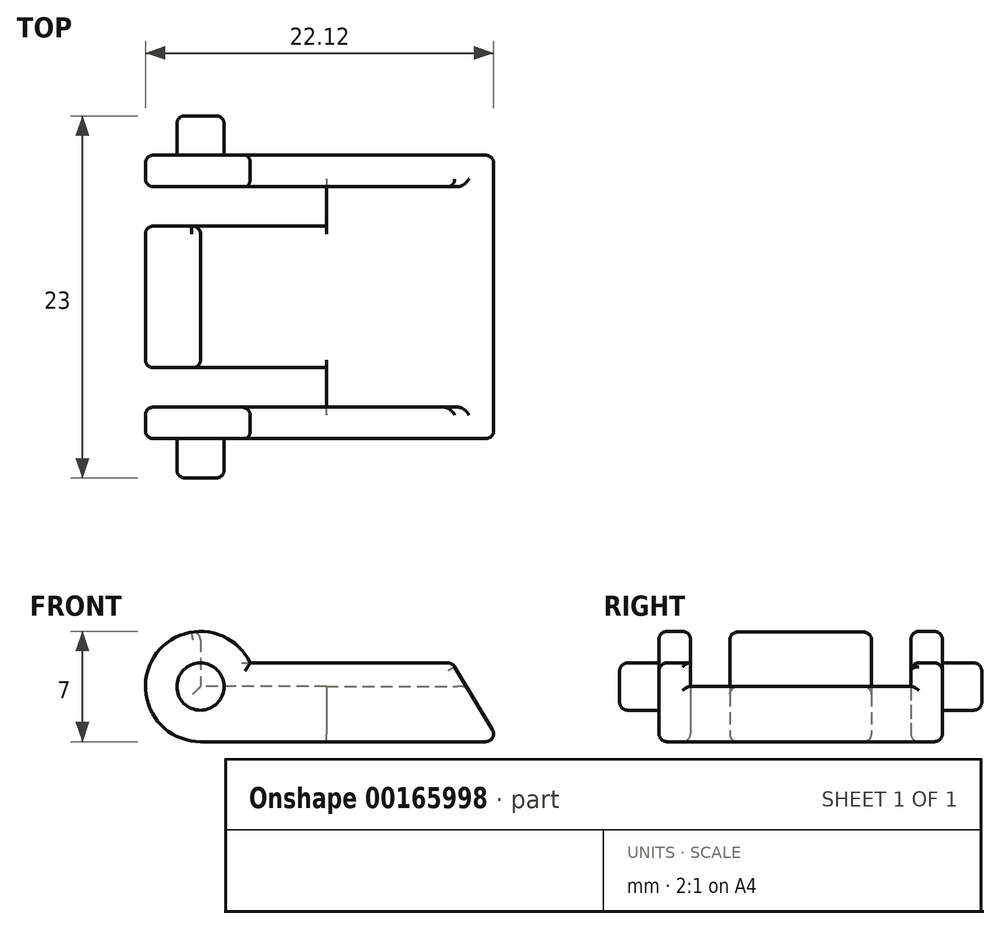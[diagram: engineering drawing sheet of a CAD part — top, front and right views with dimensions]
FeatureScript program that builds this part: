
annotation { "Feature Type Name" : "Feature", "Feature Type Description" : "" }
export const myFeature = defineFeature(function(context is Context, id is Id, definition is map)
    precondition{}
    {
        {
            var Q0;
            Q0=qCreatedBy(makeId("Front.planeOp"),FACE);
            var sketch = newSketch(context, id + "F0", { "sketchPlane" : qUnion([Q0])});
            skLineSegment(sketch, "E0.bottom", {"start": v(0, 0) * mm, "end": v(19, 0) * mm});
            skLineSegment(sketch, "E0.left", {"start": v(0, 0) * mm, "end": v(0, 5) * mm});
            skLineSegment(sketch, "E1", {"start": v(0, 5) * mm, "end": v(16, 5) * mm});
            skLineSegment(sketch, "E2", {"start": v(16, 5) * mm, "end": v(19, 0) * mm});
            skLineSegment(sketch, "E3", {"start": v(0, 0) * mm, "end": v(0, 3.5) * mm});
            skCircle(sketch, "E4", {"center": v(0, 3.5) * mm, "radius": 3.5 * mm});
            skSolve(sketch);
        }
        {
            var Q0;
            {var subQ0=sQuery(id+"F0.wireOp",EDGE,"E0.left");Q0=makeQuery(id+"F0.imprint","IMPRINT",FACE,{"disambiguationData":[TD([[makeQuery(id+"F0.imprint","IMPRINT",EDGE,{"derivedFrom":subQ0}),1.0]])]});}
            var Q1;
            {var subQ0=sQuery(id+"F0.wireOp",EDGE,"E0.left");Q1=makeQuery(id+"F0.imprint","IMPRINT",FACE,{"disambiguationData":[TD([[makeQuery(id+"F0.imprint","IMPRINT",EDGE,{"derivedFrom":subQ0}),-1.0]])]});}
            var Q2;
            {var subQ0=sQuery(id+"F0.wireOp",EDGE,"E0.bottom");Q2=makeQuery(id+"F0.imprint","IMPRINT",FACE,{"disambiguationData":[TD([[makeQuery(id+"F0.imprint","IMPRINT",EDGE,{"derivedFrom":subQ0}),1.0]])]});}
            extrude(context, id + "F1", {"entities" : qUnion([Q0, Q1, Q2]), "depth" : 18 * mm});
        }
        {
            var Q0;
            Q0=makeQuery(id+"F1.opExtrude","CAP_FACE",FACE,{"disambiguationData":[OSD([sQuery(id+"F0.wireOp",EDGE,"E0.bottom"),sQuery(id+"F0.wireOp",EDGE,"E1"),sQuery(id+"F0.wireOp",EDGE,"E2"),sQuery(id+"F0.wireOp",EDGE,"E4")])],"isStart":false});
            var sketch = newSketch(context, id + "F2", { "sketchPlane" : qUnion([Q0])});
            skCircle(sketch, "E5", {"center": v(0, 3.5) * mm, "radius": 1.5 * mm});
            skSolve(sketch);
        }
        {
            var Q0;
            Q0=makeQuery(id+"F2.imprint","IMPRINT",FACE,{"disambiguationData":[TD([[makeQuery(id+"F2.imprint","IMPRINT",EDGE,{"derivedFrom":sQuery(id+"F2.wireOp",EDGE,"E5")}),1.0]])]});
            extrude(context, id + "F3", {"entities" : qUnion([Q0]), "operationType" : NewBodyOperationType.ADD, "depth" : 2.5 * mm});
        }
        {
            var Q0;
            Q0=makeQuery(id+"F1.opExtrude","CAP_FACE",FACE,{"disambiguationData":[OSD([sQuery(id+"F0.wireOp",EDGE,"E0.bottom"),sQuery(id+"F0.wireOp",EDGE,"E1"),sQuery(id+"F0.wireOp",EDGE,"E2"),sQuery(id+"F0.wireOp",EDGE,"E4")])],"isStart":true});
            var sketch = newSketch(context, id + "F4", { "sketchPlane" : qUnion([Q0])});
            skCircle(sketch, "E6", {"center": v(0, 3.5) * mm, "radius": 1.5 * mm});
            skSolve(sketch);
        }
        {
            var Q0;
            Q0=makeQuery(id+"F4.imprint","IMPRINT",FACE,{"disambiguationData":[TD([[makeQuery(id+"F4.imprint","IMPRINT",EDGE,{"derivedFrom":sQuery(id+"F4.wireOp",EDGE,"E6")}),1.0]])]});
            extrude(context, id + "F5", {"entities" : qUnion([Q0]), "operationType" : NewBodyOperationType.ADD, "depth" : 2.5 * mm});
        }
        {
            var Q0;
            Q0=makeQuery(id+"F1.opExtrude","SWEPT_FACE",FACE,{"disambiguationData":[OSD([sQuery(id+"F0.wireOp",EDGE,"E0.bottom")])]});
            var sketch = newSketch(context, id + "F6", { "sketchPlane" : qUnion([Q0])});
            skLineSegment(sketch, "E7.bottom", {"start": v(8, 13.5) * mm, "end": v(-8, 13.5) * mm});
            skLineSegment(sketch, "E7.top", {"start": v(8, 16) * mm, "end": v(-8, 16) * mm});
            skLineSegment(sketch, "E7.left", {"start": v(8, 13.5) * mm, "end": v(8, 16) * mm});
            skLineSegment(sketch, "E7.right", {"start": v(-8, 13.5) * mm, "end": v(-8, 16) * mm});
            skPoint(sketch, "E7.middle", {"position": v(0, 14.75) * mm});
            skLineSegment(sketch, "E8.bottom", {"start": v(8, 4.5) * mm, "end": v(-8, 4.5) * mm});
            skLineSegment(sketch, "E8.top", {"start": v(8, 2) * mm, "end": v(-8, 2) * mm});
            skLineSegment(sketch, "E8.left", {"start": v(8, 4.5) * mm, "end": v(8, 2) * mm});
            skLineSegment(sketch, "E8.right", {"start": v(-8, 4.5) * mm, "end": v(-8, 2) * mm});
            skPoint(sketch, "E8.middle", {"position": v(0, 3.3) * mm});
            skSolve(sketch);
        }
        {
            var Q0;
            Q0 = qSketchRegion(id + "F6", true);
            extrude(context, id + "F7", {"entities" : qUnion([Q0]), "operationType" : NewBodyOperationType.REMOVE, "endBound" : BoundingType.THROUGH_ALL, "oppositeDirection" : true, "depth" : 25 * mm});
        }
        {
            var Q0;
            Q0=makeQuery(id+"F1.opExtrude","SWEPT_FACE",FACE,{"disambiguationData":[OSD([sQuery(id+"F0.wireOp",EDGE,"E1")])]});
            var sketch = newSketch(context, id + "F8", { "sketchPlane" : qUnion([Q0])});
            skLineSegment(sketch, "E9.bottom", {"start": v(0, -2) * mm, "end": v(18.99, -2) * mm});
            skLineSegment(sketch, "E9.top", {"start": v(0, -16) * mm, "end": v(18.99, -16) * mm});
            skLineSegment(sketch, "E9.left", {"start": v(0, -2) * mm, "end": v(0, -16) * mm});
            skLineSegment(sketch, "E9.right", {"start": v(18.99, -2) * mm, "end": v(18.99, -16) * mm});
            skSolve(sketch);
        }
        {
            var Q0;
            Q0 = qSketchRegion(id + "F8", true);
            extrude(context, id + "F9", {"entities" : qUnion([Q0]), "operationType" : NewBodyOperationType.REMOVE, "oppositeDirection" : true, "depth" : 1.5 * mm});
        }
        {
            var Q0;
            Q0=makeQuery(id+"F9.boolean.opBoolean","COPY",FACE,{"derivedFrom":makeQuery(id+"F9.opExtrude","CAP_FACE",FACE,{"disambiguationData":[OSD([sQuery(id+"F8.wireOp",EDGE,"E9.bottom"),sQuery(id+"F8.wireOp",EDGE,"E9.top"),sQuery(id+"F8.wireOp",EDGE,"E9.left"),sQuery(id+"F8.wireOp",EDGE,"E9.right")])],"isStart":false})});
            var sketch = newSketch(context, id + "F10", { "sketchPlane" : qUnion([Q0])});
            skLineSegment(sketch, "E10.bottom", {"start": v(0, -4.5) * mm, "end": v(4.86, -4.5) * mm});
            skLineSegment(sketch, "E10.top", {"start": v(0, -13.5) * mm, "end": v(4.86, -13.5) * mm});
            skLineSegment(sketch, "E10.left", {"start": v(0, -4.5) * mm, "end": v(0, -13.5) * mm});
            skLineSegment(sketch, "E10.right", {"start": v(4.86, -4.5) * mm, "end": v(4.86, -13.5) * mm});
            skSolve(sketch);
        }
        {
            var Q0;
            Q0 = qSketchRegion(id + "F10", true);
            extrude(context, id + "F11", {"entities" : qUnion([Q0]), "operationType" : NewBodyOperationType.REMOVE, "depth" : 6.3 * mm});
        }
        {
            var Q0;
            Q0=makeQuery(id+"F1.opExtrude","CAP_EDGE",EDGE,{"disambiguationData":[OSD([sQuery(id+"F0.wireOp",EDGE,"E1")])],"isStart":false});
            var Q1;
            Q1=makeQuery(id+"F1.opExtrude","CAP_EDGE",EDGE,{"disambiguationData":[OSD([sQuery(id+"F0.wireOp",EDGE,"E2")])],"isStart":false});
            var Q2;
            Q2=makeQuery(id+"F1.opExtrude","CAP_EDGE",EDGE,{"disambiguationData":[OSD([sQuery(id+"F0.wireOp",EDGE,"E0.bottom")])],"isStart":false});
            var Q3;
            Q3=makeQuery(id+"F9.boolean.opBoolean","INTERSECT",EDGE,{"derivedFrom":[makeQuery(id+"F1.opExtrude","SWEPT_FACE",FACE,{"disambiguationData":[OSD([sQuery(id+"F0.wireOp",EDGE,"E2")])]}),makeQuery(id+"F9.opExtrude","SWEPT_FACE",FACE,{"disambiguationData":[OSD([sQuery(id+"F8.wireOp",EDGE,"E9.top")])]})]});
            var Q4;
            Q4=makeQuery(id+"F9.boolean.opBoolean","INTERSECT",EDGE,{"derivedFrom":[makeQuery(id+"F1.opExtrude","SWEPT_FACE",FACE,{"disambiguationData":[OSD([sQuery(id+"F0.wireOp",EDGE,"E2")])]}),makeQuery(id+"F9.opExtrude","CAP_FACE",FACE,{"disambiguationData":[OSD([sQuery(id+"F8.wireOp",EDGE,"E9.bottom"),sQuery(id+"F8.wireOp",EDGE,"E9.top"),sQuery(id+"F8.wireOp",EDGE,"E9.left"),sQuery(id+"F8.wireOp",EDGE,"E9.right")])],"isStart":false})]});
            var Q5;
            {var subQ0=sQuery(id+"F0.wireOp",EDGE,"E2");var subQ1=sQuery(id+"F0.wireOp",EDGE,"E1");Q5=makeQuery(id+"F9.boolean.opBoolean","SPLIT",EDGE,{"disambiguationData":[TD([makeQuery(id+"F9.opExtrude","SWEPT_FACE",FACE,{"disambiguationData":[OSD([sQuery(id+"F8.wireOp",EDGE,"E9.top")])]})])],"derivedFrom":makeQuery(id+"F1.opExtrude","SWEPT_EDGE",EDGE,{"disambiguationData":[OSD([subQ1,subQ0])]})});}
            var Q6;
            Q6=makeQuery(id+"F9.boolean.opBoolean","INTERSECT",EDGE,{"derivedFrom":[makeQuery(id+"F7.boolean.opBoolean","COPY",FACE,{"derivedFrom":makeQuery(id+"F7.opExtrude","SWEPT_FACE",FACE,{"disambiguationData":[OSD([sQuery(id+"F6.wireOp",EDGE,"E7.bottom")])]})}),makeQuery(id+"F9.opExtrude","CAP_FACE",FACE,{"disambiguationData":[OSD([sQuery(id+"F8.wireOp",EDGE,"E9.bottom"),sQuery(id+"F8.wireOp",EDGE,"E9.top"),sQuery(id+"F8.wireOp",EDGE,"E9.left"),sQuery(id+"F8.wireOp",EDGE,"E9.right")])],"isStart":false})]});
            var Q7;
            Q7=makeQuery(id+"F11.boolean.opBoolean","MERGE",EDGE,{"derivedFrom":[makeQuery(id+"F9.boolean.opBoolean","INTERSECT",EDGE,{"derivedFrom":[makeQuery(id+"F7.boolean.opBoolean","COPY",FACE,{"derivedFrom":makeQuery(id+"F7.opExtrude","SWEPT_FACE",FACE,{"disambiguationData":[OSD([sQuery(id+"F6.wireOp",EDGE,"E7.bottom")])]})}),makeQuery(id+"F9.opExtrude","SWEPT_FACE",FACE,{"disambiguationData":[OSD([sQuery(id+"F8.wireOp",EDGE,"E9.left")])]})]}),makeQuery(id+"F11.opExtrude","SWEPT_EDGE",EDGE,{"disambiguationData":[OSD([sQuery(id+"F10.wireOp",EDGE,"E10.top"),sQuery(id+"F10.wireOp",EDGE,"E10.left")])]})]});
            var Q8;
            Q8=makeQuery(id+"F11.boolean.opBoolean","MERGE",EDGE,{"derivedFrom":[makeQuery(id+"F9.boolean.opBoolean","INTERSECT",EDGE,{"derivedFrom":[makeQuery(id+"F7.boolean.opBoolean","COPY",FACE,{"derivedFrom":makeQuery(id+"F7.opExtrude","SWEPT_FACE",FACE,{"disambiguationData":[OSD([sQuery(id+"F6.wireOp",EDGE,"E8.bottom")])]})}),makeQuery(id+"F9.opExtrude","SWEPT_FACE",FACE,{"disambiguationData":[OSD([sQuery(id+"F8.wireOp",EDGE,"E9.left")])]})]}),makeQuery(id+"F11.opExtrude","SWEPT_EDGE",EDGE,{"disambiguationData":[OSD([sQuery(id+"F10.wireOp",EDGE,"E10.bottom"),sQuery(id+"F10.wireOp",EDGE,"E10.left")])]})]});
            var Q9;
            Q9=makeQuery(id+"F9.boolean.opBoolean","INTERSECT",EDGE,{"derivedFrom":[makeQuery(id+"F7.boolean.opBoolean","COPY",FACE,{"derivedFrom":makeQuery(id+"F7.opExtrude","SWEPT_FACE",FACE,{"disambiguationData":[OSD([sQuery(id+"F6.wireOp",EDGE,"E8.bottom")])]})}),makeQuery(id+"F9.opExtrude","CAP_FACE",FACE,{"disambiguationData":[OSD([sQuery(id+"F8.wireOp",EDGE,"E9.bottom"),sQuery(id+"F8.wireOp",EDGE,"E9.top"),sQuery(id+"F8.wireOp",EDGE,"E9.left"),sQuery(id+"F8.wireOp",EDGE,"E9.right")])],"isStart":false})]});
            var Q10;
            {var subQ0=sQuery(id+"F0.wireOp",EDGE,"E2");var subQ1=sQuery(id+"F0.wireOp",EDGE,"E1");Q10=makeQuery(id+"F9.boolean.opBoolean","SPLIT",EDGE,{"disambiguationData":[TD([makeQuery(id+"F9.opExtrude","SWEPT_FACE",FACE,{"disambiguationData":[OSD([sQuery(id+"F8.wireOp",EDGE,"E9.bottom")])]})])],"derivedFrom":makeQuery(id+"F1.opExtrude","SWEPT_EDGE",EDGE,{"disambiguationData":[OSD([subQ1,subQ0])]})});}
            var Q11;
            Q11=makeQuery(id+"F1.opExtrude","CAP_EDGE",EDGE,{"disambiguationData":[OSD([sQuery(id+"F0.wireOp",EDGE,"E2")])],"isStart":true});
            var Q12;
            Q12=makeQuery(id+"F1.opExtrude","SWEPT_EDGE",EDGE,{"disambiguationData":[OSD([sQuery(id+"F0.wireOp",EDGE,"E0.bottom"),sQuery(id+"F0.wireOp",EDGE,"E2")])]});
            var Q13;
            Q13=makeQuery(id+"F9.boolean.opBoolean","INTERSECT",EDGE,{"derivedFrom":[makeQuery(id+"F1.opExtrude","SWEPT_FACE",FACE,{"disambiguationData":[OSD([sQuery(id+"F0.wireOp",EDGE,"E2")])]}),makeQuery(id+"F9.opExtrude","SWEPT_FACE",FACE,{"disambiguationData":[OSD([sQuery(id+"F8.wireOp",EDGE,"E9.bottom")])]})]});
            var Q14;
            Q14=makeQuery(id+"F1.opExtrude","CAP_EDGE",EDGE,{"disambiguationData":[OSD([sQuery(id+"F0.wireOp",EDGE,"E1")])],"isStart":true});
            var Q15;
            Q15=makeQuery(id+"F1.opExtrude","CAP_EDGE",EDGE,{"disambiguationData":[OSD([sQuery(id+"F0.wireOp",EDGE,"E4")])],"isStart":true});
            var Q16;
            Q16=makeQuery(id+"F7.boolean.opBoolean","INTERSECT",EDGE,{"derivedFrom":[makeQuery(id+"F1.opExtrude","SWEPT_FACE",FACE,{"disambiguationData":[OSD([sQuery(id+"F0.wireOp",EDGE,"E4")])]}),makeQuery(id+"F7.opExtrude","SWEPT_FACE",FACE,{"disambiguationData":[OSD([sQuery(id+"F6.wireOp",EDGE,"E7.top")])]})]});
            var Q17;
            Q17=makeQuery(id+"F7.boolean.opBoolean","INTERSECT",EDGE,{"derivedFrom":[makeQuery(id+"F1.opExtrude","SWEPT_FACE",FACE,{"disambiguationData":[OSD([sQuery(id+"F0.wireOp",EDGE,"E4")])]}),makeQuery(id+"F7.opExtrude","SWEPT_FACE",FACE,{"disambiguationData":[OSD([sQuery(id+"F6.wireOp",EDGE,"E8.top")])]})]});
            var Q18;
            Q18=makeQuery(id+"F3.opExtrude","CAP_EDGE",EDGE,{"disambiguationData":[OSD([sQuery(id+"F2.wireOp",EDGE,"E5")])],"isStart":false});
            var Q19;
            Q19=makeQuery(id+"F5.opExtrude","CAP_EDGE",EDGE,{"disambiguationData":[OSD([sQuery(id+"F4.wireOp",EDGE,"E6")])],"isStart":false});
            var Q20;
            Q20=makeQuery(id+"F7.boolean.opBoolean","INTERSECT",EDGE,{"derivedFrom":[makeQuery(id+"F1.opExtrude","SWEPT_FACE",FACE,{"disambiguationData":[OSD([sQuery(id+"F0.wireOp",EDGE,"E4")])]}),makeQuery(id+"F7.opExtrude","SWEPT_FACE",FACE,{"disambiguationData":[OSD([sQuery(id+"F6.wireOp",EDGE,"E8.bottom")])]})]});
            var Q21;
            Q21=makeQuery(id+"F7.boolean.opBoolean","INTERSECT",EDGE,{"derivedFrom":[makeQuery(id+"F1.opExtrude","SWEPT_FACE",FACE,{"disambiguationData":[OSD([sQuery(id+"F0.wireOp",EDGE,"E4")])]}),makeQuery(id+"F7.opExtrude","SWEPT_FACE",FACE,{"disambiguationData":[OSD([sQuery(id+"F6.wireOp",EDGE,"E7.bottom")])]})]});
            fillet(context, id + "F12", {"entities" : qUnion([Q0, Q1, Q2, Q3, Q4, Q5, Q6, Q7, Q8, Q9, Q10, Q11, Q12, Q13, Q14, Q15, Q16, Q17, Q18, Q19, Q20, Q21]), "radius" : .5 * mm, "tangentPropagation" : true, "allowEdgeOverflow" : false});
        }
        {
            var Q0;
            Q0=makeQuery(id+"F7.boolean.opBoolean","INTERSECT",EDGE,{"derivedFrom":[makeQuery(id+"F1.opExtrude","SWEPT_FACE",FACE,{"disambiguationData":[OSD([sQuery(id+"F0.wireOp",EDGE,"E1")])]}),makeQuery(id+"F7.opExtrude","SWEPT_FACE",FACE,{"disambiguationData":[OSD([sQuery(id+"F6.wireOp",EDGE,"E8.top")])]})]});
            var Q1;
            Q1=makeQuery(id+"F9.boolean.opBoolean","MERGE",EDGE,{"derivedFrom":[makeQuery(id+"F7.boolean.opBoolean","INTERSECT",EDGE,{"derivedFrom":[makeQuery(id+"F1.opExtrude","SWEPT_FACE",FACE,{"disambiguationData":[OSD([sQuery(id+"F0.wireOp",EDGE,"E1")])]}),makeQuery(id+"F7.opExtrude","SWEPT_FACE",FACE,{"disambiguationData":[OSD([sQuery(id+"F6.wireOp",EDGE,"E7.top")])]})]}),makeQuery(id+"F9.opExtrude","CAP_EDGE",EDGE,{"disambiguationData":[OSD([sQuery(id+"F8.wireOp",EDGE,"E9.top")])],"isStart":true})]});
            fillet(context, id + "F13", {"entities" : qUnion([Q0, Q1]), "radius" : .5 * mm, "tangentPropagation" : true, "allowEdgeOverflow" : false});
        }
        {
            var Q0;
            Q0=makeQuery(id+"F11.boolean.opBoolean","INTERSECT",EDGE,{"derivedFrom":[makeQuery(id+"F7.boolean.opBoolean","SPLIT",FACE,{"disambiguationData":[TD([makeQuery(id+"F7.opExtrude","SWEPT_FACE",FACE,{"disambiguationData":[OSD([sQuery(id+"F6.wireOp",EDGE,"E7.bottom")])]})])],"derivedFrom":makeQuery(id+"F1.opExtrude","SWEPT_FACE",FACE,{"disambiguationData":[OSD([sQuery(id+"F0.wireOp",EDGE,"E4")])]})}),makeQuery(id+"F11.opExtrude","SWEPT_FACE",FACE,{"disambiguationData":[OSD([sQuery(id+"F10.wireOp",EDGE,"E10.left")])]})]});
            fillet(context, id + "F14", {"entities" : qUnion([Q0]), "radius" : .5 * mm, "tangentPropagation" : true, "allowEdgeOverflow" : false});
        }
    });
